# Revit family: Faucet-Lavatory-American_Standard-Studio_S-7105152.sss
name_source: partatom
category: Plumbing Fixtures
units: mm (PartAtom-declared; Revit-internal decimal feet)

## family parameters
Always vertical = No
Cut with Voids When Loaded = No
OmniClass Number = 23.45.55.14
OmniClass Title = Single Faucets
Part Type = Normal
Room Calculation Point = No
Round Connector Dimension = Use Diameter
Shared = Yes
Work Plane-Based = Yes

## types (1)
- 7105.152.243
    ADA Compliant = Yes
    Assembly Code = D2020300
    CEC Compliant = Yes
    CW Connection = No
    CWFU = 1.5
    CalGreen Compliant = Yes
    Compliance Certifications = ANSI A117.1, ASME A112.18.1, CSA B125.1, NSF 61/Section 9 & NSF 372
    Default Elevation = 0"
    Description = Studio® S Single Hole Single-Handle Vessel Sink Faucet 1.2 gpm/4.5 L/min With Lever Handle
    EPA WaterSense® Certified = Yes
    Finish = Metal-American Standard-243-Matte Black
    Flow Rate = 1.2 gpm/4.5 L/min
    HW Connection = No
    HWFU = 1.5
    Height = 13 9/16"
    Installation Type = Deck Mounted
    Length = 7 1/16"
    Manufacturer = American Standard
    Material = Metal-American Standard-243-Matte Black
    Metal Grid Drain Depth = 5 1/2"
    Metal Grid Drain Distance from Faucet Centre = 6 1/2"
    Metal Grid Drain Included = Yes
    Model = 7105.152.243
    Price = Prices may vary. Please consult Manufacturer Representative for most up-to-date price list.
    Product Documentation Link = https://americanstandard.box.com
    Product Page URL = https://americanstandard.ca
    Revised Date = 07/25/2022
    Tempered Water Connection = Yes
    Tempered Water Connection Diameter = 3/8"
    URL = https://americanstandard.ca
    Vent Connection = No
    WFU = 2
    Warranty Information = Limited Lifetime Warrany on function and finish.
    Waste Connection = No
    Width = 1 1/4"

## geometry (parser evidence)
native form markers: Sweep x2
no freeform markers — native parametric forms only
